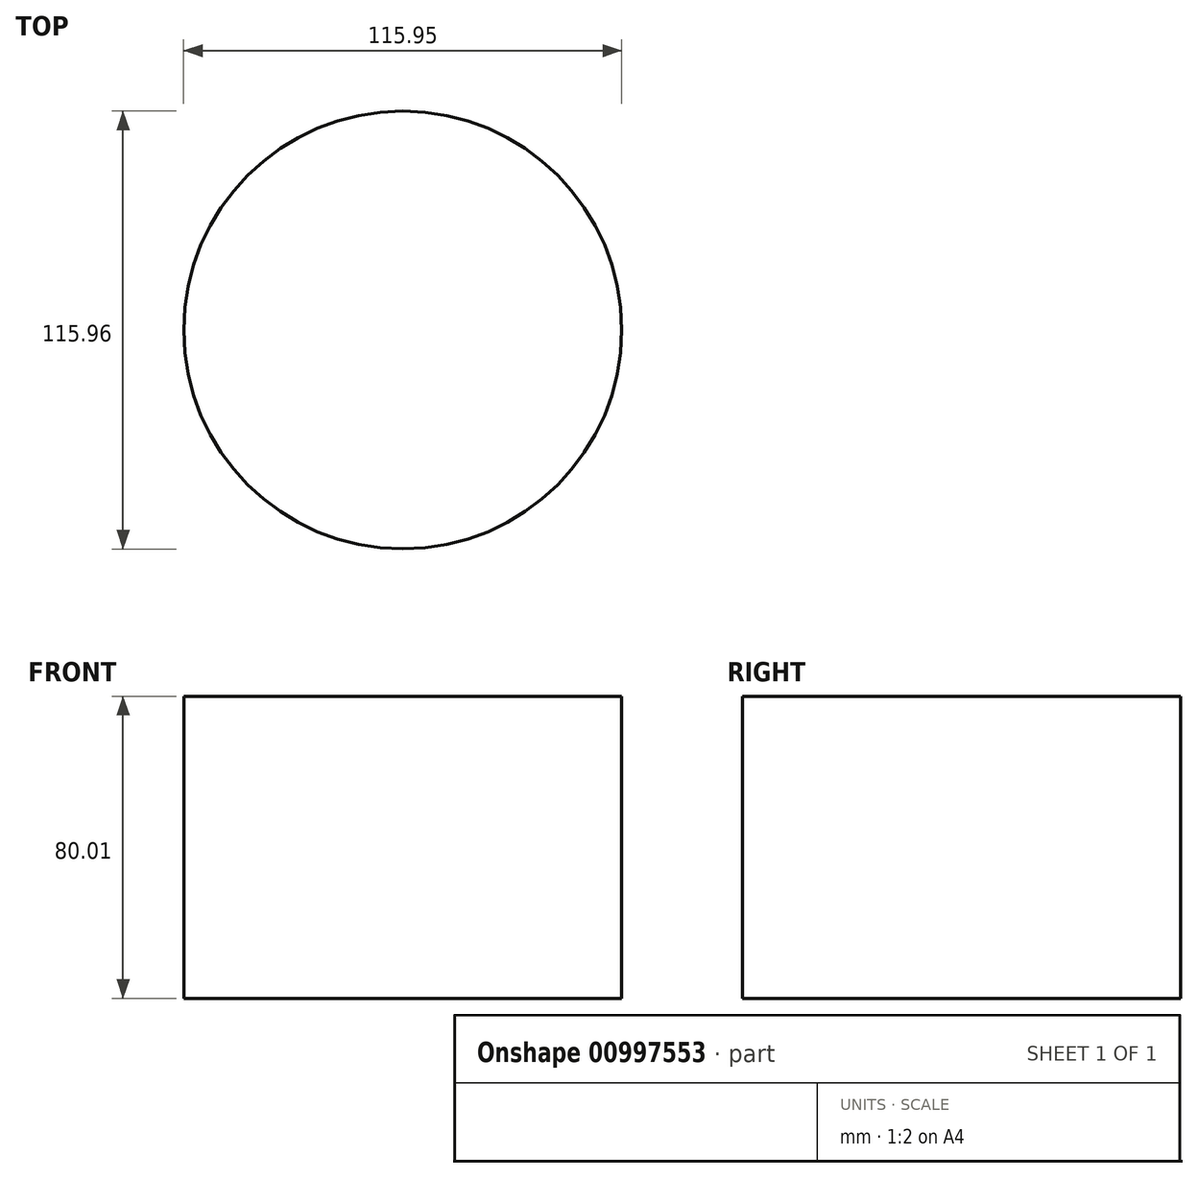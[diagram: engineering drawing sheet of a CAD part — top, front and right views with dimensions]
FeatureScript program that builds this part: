
annotation { "Feature Type Name" : "Feature", "Feature Type Description" : "" }
export const myFeature = defineFeature(function(context is Context, id is Id, definition is map)
    precondition{}
    {
        {
            var Q0;
            Q0=qCreatedBy(makeId("Top.planeOp"),FACE);
            var sketch = newSketch(context, id + "F0", { "sketchPlane" : qUnion([Q0])});
            skCircle(sketch, "E0", {"center": v(-4.9, 0) * mm, "radius": 57.98 * mm});
            skSolve(sketch);
        }
        {
            var Q0;
            Q0=makeQuery(id+"F0.imprint","IMPRINT",FACE,{"disambiguationData":[TD([[makeQuery(id+"F0.imprint","IMPRINT",EDGE,{"derivedFrom":sQuery(id+"F0.wireOp",EDGE,"E0")}),1.0]])]});
            extrude(context, id + "F1", {"entities" : qUnion([Q0]), "depth" : 80 * mm, "offsetDistance" : 25.4 * mm});
        }
    });
